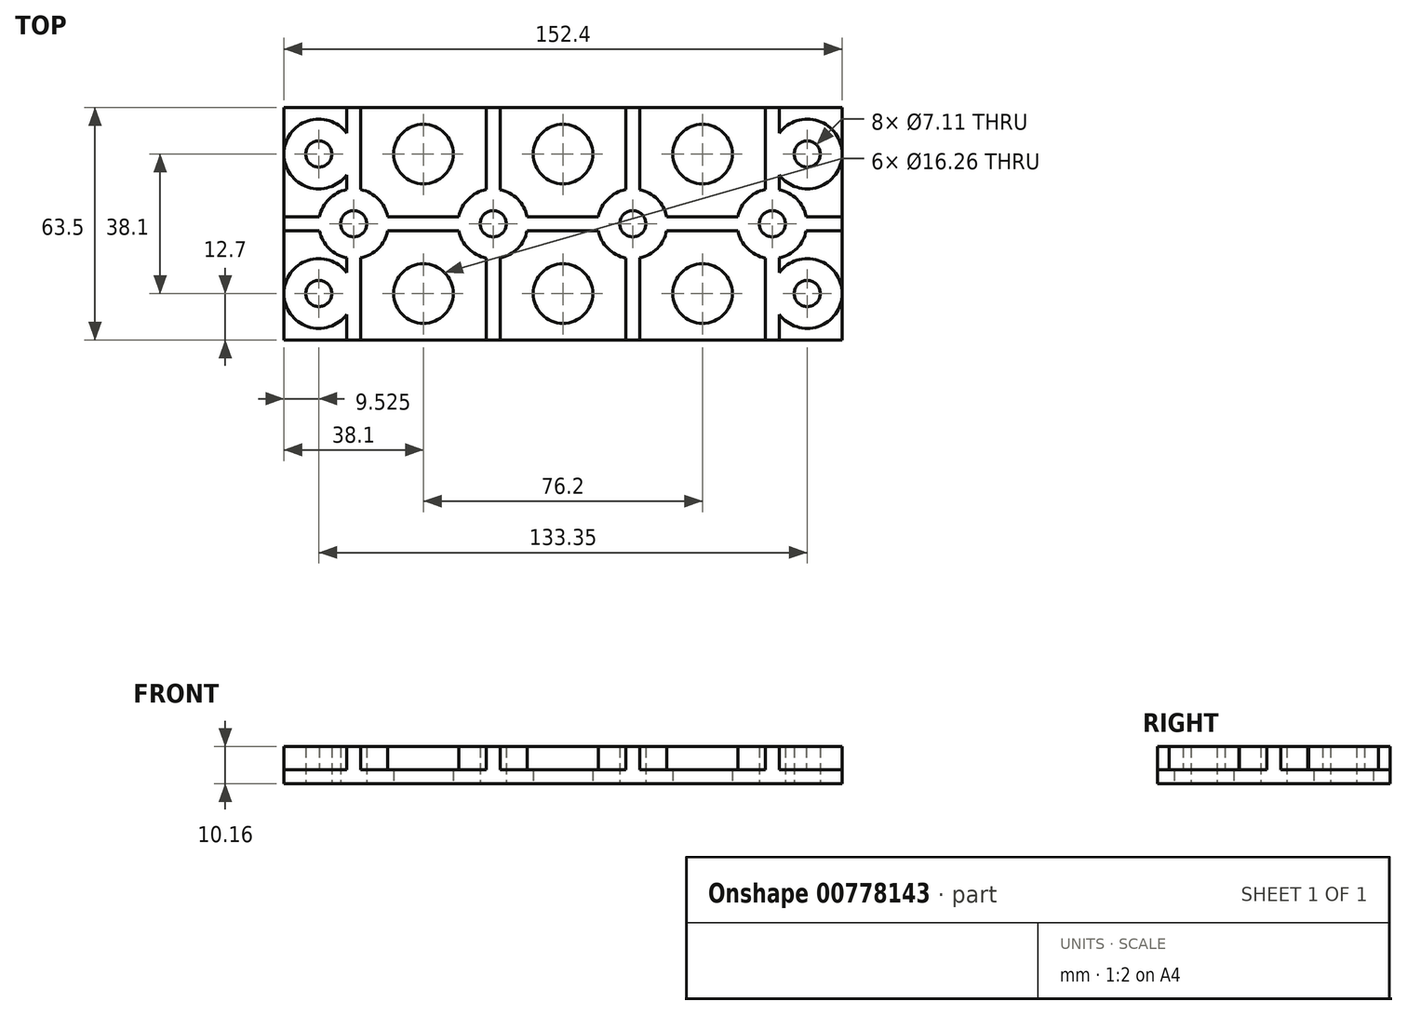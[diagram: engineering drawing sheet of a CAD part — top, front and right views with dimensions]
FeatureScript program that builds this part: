
annotation { "Feature Type Name" : "Feature", "Feature Type Description" : "" }
export const myFeature = defineFeature(function(context is Context, id is Id, definition is map)
    precondition{}
    {
        {
            var Q0;
            Q0=qCreatedBy(makeId("Top.planeOp"),FACE);
            var sketch = newSketch(context, id + "F0", { "sketchPlane" : qUnion([Q0])});
            skLineSegment(sketch, "E0.bottom", {"start": v(0, 0) * mm, "end": v(152.4, 0) * mm});
            skLineSegment(sketch, "E0.top", {"start": v(0, 63.5) * mm, "end": v(152.4, 63.5) * mm});
            skLineSegment(sketch, "E0.left", {"start": v(0, 0) * mm, "end": v(0, 63.5) * mm});
            skLineSegment(sketch, "E0.right", {"start": v(152.4, 0) * mm, "end": v(152.4, 63.5) * mm});
            skSolve(sketch);
        }
        {
            var Q0;
            Q0 = qSketchRegion(id + "F0", true);
            extrude(context, id + "F1", {"entities" : qUnion([Q0]), "depth" : 3.8 * mm, "offsetDistance" : 25.4 * mm});
        }
        {
            var Q0;
            Q0=qCreatedBy(makeId("Top.planeOp"),FACE);
            var sketch = newSketch(context, id + "F2", { "sketchPlane" : qUnion([Q0])});
            skCircle(sketch, "E1", {"center": v(38.1, 12.7) * mm, "radius": 8.13 * mm});
            skCircle(sketch, "E2", {"center": v(38.1, 50.8) * mm, "radius": 8.13 * mm});
            skCircle(sketch, "E3", {"center": v(76.2, 50.8) * mm, "radius": 8.13 * mm});
            skCircle(sketch, "E4", {"center": v(76.2, 12.7) * mm, "radius": 8.13 * mm});
            skCircle(sketch, "E5", {"center": v(114.3, 50.8) * mm, "radius": 8.13 * mm});
            skCircle(sketch, "E6", {"center": v(114.3, 12.7) * mm, "radius": 8.13 * mm});
            skSolve(sketch);
        }
        {
            var Q0;
            Q0 = qSketchRegion(id + "F2", true);
            extrude(context, id + "F3", {"entities" : qUnion([Q0]), "operationType" : NewBodyOperationType.REMOVE, "endBound" : BoundingType.THROUGH_ALL, "depth" : 25.4 * mm, "offsetDistance" : 25.4 * mm});
        }
        {
            var Q0;
            Q0=qCreatedBy(makeId("Top.planeOp"),FACE);
            var sketch = newSketch(context, id + "F4", { "sketchPlane" : qUnion([Q0])});
            skLineSegment(sketch, "E7", {"start": v(0, 31.75) * mm, "end": v(127, 31.75) * mm, "construction": true});
            skPoint(sketch, "E7.startSnap0", {"position": v(127, 31.75) * mm});
            skLineSegment(sketch, "E8", {"start": v(57.15, 76.2) * mm, "end": v(57.15, 0) * mm, "construction": true});
            skLineSegment(sketch, "E9", {"start": v(95.25, 76.2) * mm, "end": v(95.25, 0) * mm, "construction": true});
            skLineSegment(sketch, "E10.bottom", {"start": v(55.25, 63.5) * mm, "end": v(59.06, 63.5) * mm});
            skLineSegment(sketch, "E10.top", {"start": v(55.25, 0) * mm, "end": v(59.06, 0) * mm});
            skLineSegment(sketch, "E10.left", {"start": v(55.25, 63.5) * mm, "end": v(55.25, 33.66) * mm});
            skLineSegment(sketch, "E10.right", {"start": v(59.06, 63.5) * mm, "end": v(59.06, 33.66) * mm});
            skLineSegment(sketch, "E11.bottom", {"start": v(93.34, 63.5) * mm, "end": v(97.16, 63.5) * mm});
            skLineSegment(sketch, "E11.top", {"start": v(93.34, 0) * mm, "end": v(97.16, 0) * mm});
            skLineSegment(sketch, "E11.left", {"start": v(93.34, 63.5) * mm, "end": v(93.34, 33.66) * mm});
            skLineSegment(sketch, "E11.right", {"start": v(97.16, 63.5) * mm, "end": v(97.16, 33.66) * mm});
            skLineSegment(sketch, "E12.bottom", {"start": v(0, 33.65) * mm, "end": v(17.15, 33.66) * mm});
            skLineSegment(sketch, "E12.top", {"start": v(0, 29.84) * mm, "end": v(17.15, 29.84) * mm});
            skLineSegment(sketch, "E12.left", {"start": v(0, 33.66) * mm, "end": v(0, 29.84) * mm});
            skLineSegment(sketch, "E12.right", {"start": v(152.4, 33.66) * mm, "end": v(152.4, 29.85) * mm});
            skLineSegment(sketch, "E13.trimOffspring", {"start": v(97.16, 33.66) * mm, "end": v(131.44, 33.66) * mm});
            skLineSegment(sketch, "E14.trimOffspring", {"start": v(93.34, 29.85) * mm, "end": v(93.34, 0) * mm});
            skLineSegment(sketch, "E15.trimOffspring", {"start": v(97.16, 29.85) * mm, "end": v(131.44, 29.85) * mm});
            skLineSegment(sketch, "E16.trimOffspring", {"start": v(97.16, 29.85) * mm, "end": v(97.16, 0) * mm});
            skLineSegment(sketch, "E17.trimOffspring", {"start": v(59.06, 33.66) * mm, "end": v(93.34, 33.66) * mm});
            skLineSegment(sketch, "E18.trimOffspring", {"start": v(59.06, 29.84) * mm, "end": v(59.06, 0) * mm});
            skLineSegment(sketch, "E19.trimOffspring", {"start": v(55.25, 29.84) * mm, "end": v(55.25, 0) * mm});
            skLineSegment(sketch, "E20.trimOffspring", {"start": v(59.06, 29.84) * mm, "end": v(93.34, 29.85) * mm});
            skLineSegment(sketch, "E21.0", {"start": v(152.4, 0) * mm, "end": v(152.4, 63.5) * mm, "construction": true});
            skLineSegment(sketch, "E22.0", {"start": v(0, 63.5) * mm, "end": v(152.4, 63.5) * mm, "construction": true});
            skLineSegment(sketch, "E23", {"start": v(19.05, 63.5) * mm, "end": v(19.05, 0) * mm, "construction": true});
            skLineSegment(sketch, "E24", {"start": v(133.35, 63.5) * mm, "end": v(133.35, 0) * mm, "construction": true});
            skLineSegment(sketch, "E25.bottom", {"start": v(17.15, 63.5) * mm, "end": v(20.96, 63.5) * mm});
            skLineSegment(sketch, "E25.top", {"start": v(17.15, 0) * mm, "end": v(20.96, 0) * mm});
            skLineSegment(sketch, "E25.left", {"start": v(17.15, 63.5) * mm, "end": v(17.15, 33.66) * mm});
            skLineSegment(sketch, "E25.right", {"start": v(20.96, 63.5) * mm, "end": v(20.96, 33.66) * mm});
            skLineSegment(sketch, "E26.bottom", {"start": v(131.44, 63.5) * mm, "end": v(135.25, 63.5) * mm});
            skLineSegment(sketch, "E26.top", {"start": v(131.44, 0) * mm, "end": v(135.25, 0) * mm});
            skLineSegment(sketch, "E26.left", {"start": v(131.44, 63.5) * mm, "end": v(131.44, 33.66) * mm});
            skLineSegment(sketch, "E26.right", {"start": v(135.25, 63.5) * mm, "end": v(135.25, 33.66) * mm});
            skLineSegment(sketch, "E27.trimOffspring", {"start": v(135.25, 33.66) * mm, "end": v(152.4, 33.66) * mm});
            skLineSegment(sketch, "E28.trimOffspring", {"start": v(135.25, 29.85) * mm, "end": v(135.25, 0) * mm});
            skLineSegment(sketch, "E29.trimOffspring", {"start": v(135.25, 29.85) * mm, "end": v(152.4, 29.85) * mm});
            skLineSegment(sketch, "E30.trimOffspring", {"start": v(131.44, 29.85) * mm, "end": v(131.44, 0) * mm});
            skLineSegment(sketch, "E31.trimOffspring", {"start": v(20.96, 33.66) * mm, "end": v(55.25, 33.66) * mm});
            skLineSegment(sketch, "E32.trimOffspring", {"start": v(17.15, 29.84) * mm, "end": v(17.15, 0) * mm});
            skLineSegment(sketch, "E33.trimOffspring", {"start": v(20.96, 29.84) * mm, "end": v(20.96, 0) * mm});
            skLineSegment(sketch, "E34.trimOffspring", {"start": v(20.96, 29.84) * mm, "end": v(55.25, 29.84) * mm});
            skSolve(sketch);
        }
        {
            var Q0;
            Q0 = qSketchRegion(id + "F4", true);
            extrude(context, id + "F5", {"entities" : qUnion([Q0]), "operationType" : NewBodyOperationType.ADD, "depth" : 10.16 * mm, "offsetDistance" : 25.4 * mm});
        }
        {
            var Q0;
            Q0=qCreatedBy(makeId("Top.planeOp"),FACE);
            var sketch = newSketch(context, id + "F6", { "sketchPlane" : qUnion([Q0])});
            skCircle(sketch, "E35", {"center": v(9.53, 50.8) * mm, "radius": 3.56 * mm});
            skCircle(sketch, "E36", {"center": v(9.53, 12.7) * mm, "radius": 3.56 * mm});
            skCircle(sketch, "E37", {"center": v(142.88, 12.7) * mm, "radius": 3.56 * mm});
            skCircle(sketch, "E38", {"center": v(142.88, 50.8) * mm, "radius": 3.56 * mm});
            skSolve(sketch);
        }
        {
            var Q0;
            Q0 = qSketchRegion(id + "F6", true);
            extrude(context, id + "F7", {"entities" : qUnion([Q0]), "operationType" : NewBodyOperationType.REMOVE, "endBound" : BoundingType.THROUGH_ALL, "depth" : 25.4 * mm, "offsetDistance" : 25.4 * mm});
        }
        {
            var Q0;
            Q0=qCreatedBy(makeId("Top.planeOp"),FACE);
            var sketch = newSketch(context, id + "F8", { "sketchPlane" : qUnion([Q0])});
            skCircle(sketch, "E39", {"center": v(57.07, 31.75) * mm, "radius": 9.53 * mm});
            skCircle(sketch, "E40", {"center": v(95.17, 31.75) * mm, "radius": 9.53 * mm});
            skCircle(sketch, "E41", {"center": v(19.05, 31.75) * mm, "radius": 9.53 * mm});
            skCircle(sketch, "E42", {"center": v(133.27, 31.75) * mm, "radius": 9.53 * mm});
            skSolve(sketch);
        }
        {
            var Q0;
            Q0 = qSketchRegion(id + "F8", true);
            extrude(context, id + "F9", {"entities" : qUnion([Q0]), "operationType" : NewBodyOperationType.ADD, "depth" : 10.16 * mm, "offsetDistance" : 25.4 * mm});
        }
        {
            var Q0;
            Q0=qCreatedBy(makeId("Top.planeOp"),FACE);
            var sketch = newSketch(context, id + "F10", { "sketchPlane" : qUnion([Q0])});
            skCircle(sketch, "E43.0", {"center": v(9.53, 50.8) * mm, "radius": 3.56 * mm});
            skCircle(sketch, "E44.0", {"center": v(9.53, 12.7) * mm, "radius": 3.56 * mm});
            skCircle(sketch, "E45.0", {"center": v(142.88, 50.8) * mm, "radius": 3.56 * mm});
            skCircle(sketch, "E46.0", {"center": v(142.88, 12.7) * mm, "radius": 3.56 * mm});
            skCircle(sketch, "E47", {"center": v(9.53, 50.8) * mm, "radius": 9.53 * mm});
            skCircle(sketch, "E48", {"center": v(9.53, 12.7) * mm, "radius": 9.53 * mm});
            skCircle(sketch, "E49", {"center": v(142.88, 50.8) * mm, "radius": 9.53 * mm});
            skCircle(sketch, "E50", {"center": v(142.88, 12.7) * mm, "radius": 9.53 * mm});
            skSolve(sketch);
        }
        {
            var Q0;
            Q0 = qSketchRegion(id + "F10", true);
            extrude(context, id + "F11", {"entities" : qUnion([Q0]), "operationType" : NewBodyOperationType.ADD, "depth" : 10.16 * mm, "offsetDistance" : 25.4 * mm});
        }
        {
            var Q0;
            Q0=qCreatedBy(makeId("Top.planeOp"),FACE);
            var sketch = newSketch(context, id + "F12", { "sketchPlane" : qUnion([Q0])});
            skCircle(sketch, "E51", {"center": v(19.05, 31.75) * mm, "radius": 3.56 * mm});
            skCircle(sketch, "E52", {"center": v(57.15, 31.75) * mm, "radius": 3.56 * mm});
            skCircle(sketch, "E53", {"center": v(95.25, 31.75) * mm, "radius": 3.56 * mm});
            skCircle(sketch, "E54", {"center": v(133.35, 31.75) * mm, "radius": 3.56 * mm});
            skSolve(sketch);
        }
        {
            var Q0;
            Q0 = qSketchRegion(id + "F12", true);
            extrude(context, id + "F13", {"entities" : qUnion([Q0]), "operationType" : NewBodyOperationType.REMOVE, "endBound" : BoundingType.THROUGH_ALL, "depth" : 25.4 * mm, "offsetDistance" : 25.4 * mm});
        }
    });
